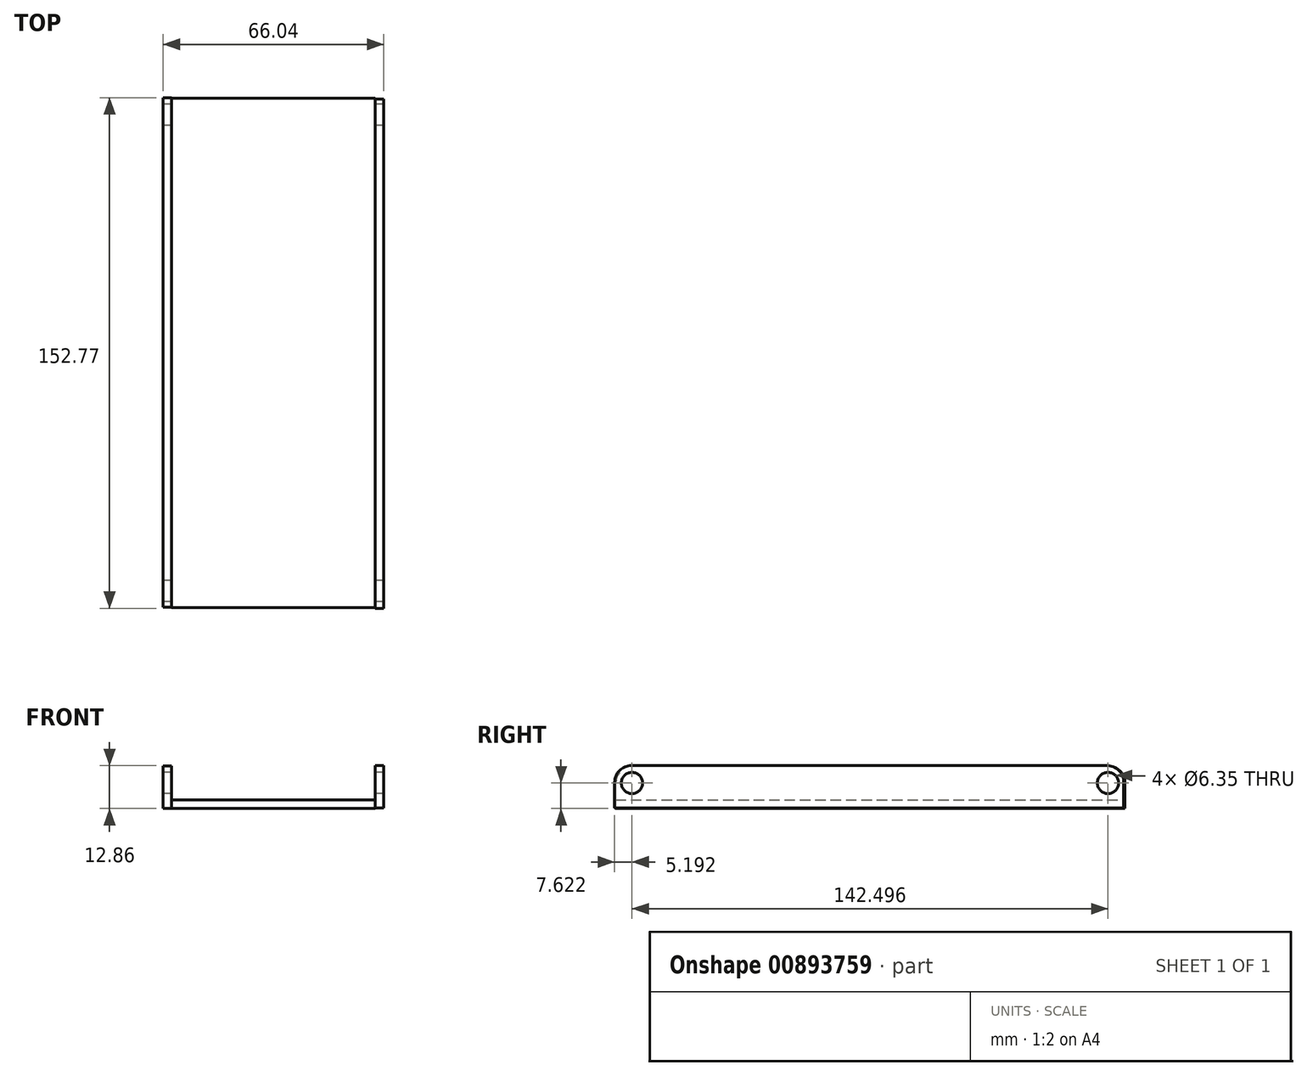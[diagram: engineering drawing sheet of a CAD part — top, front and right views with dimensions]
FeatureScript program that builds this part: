
annotation { "Feature Type Name" : "Feature", "Feature Type Description" : "" }
export const myFeature = defineFeature(function(context is Context, id is Id, definition is map)
    precondition{}
    {
        {
            var Q0;
            Q0=qCreatedBy(makeId("Top.planeOp"),FACE);
            var sketch = newSketch(context, id + "F0", { "sketchPlane" : qUnion([Q0])});
            skLineSegment(sketch, "E0.bottom", {"start": v(30.48, -76.2) * mm, "end": v(-30.48, -76.2) * mm});
            skLineSegment(sketch, "E0.top", {"start": v(30.48, 76.2) * mm, "end": v(-30.48, 76.2) * mm});
            skLineSegment(sketch, "E0.left", {"start": v(30.48, -76.2) * mm, "end": v(30.48, 76.2) * mm});
            skLineSegment(sketch, "E0.right", {"start": v(-30.48, -76.2) * mm, "end": v(-30.48, 76.2) * mm});
            skPoint(sketch, "E0.middle", {"position": v(0, 0) * mm});
            skSolve(sketch);
        }
        {
            var Q0;
            Q0=qSketchRegion(id+"F0",true);
            extrude(context, id + "F1", {"entities" : qUnion([Q0]), "depth" : 2.54 * mm, "offsetDistance" : 25.4 * mm});
        }
        {
            var Q0;
            Q0=makeQuery(id+"F1.opExtrude","SWEPT_FACE",FACE,{"disambiguationData":[OSD([sQuery(id+"F0.wireOp",EDGE,"E0.left")])]});
            var sketch = newSketch(context, id + "F2", { "sketchPlane" : qUnion([Q0])});
            skLineSegment(sketch, "E1.bottom", {"start": v(75.96, 0.1) * mm, "end": v(-76.44, 0.1) * mm});
            skLineSegment(sketch, "E1.top", {"start": v(75.96, 12.8) * mm, "end": v(-76.44, 12.8) * mm});
            skLineSegment(sketch, "E1.left", {"start": v(75.96, 0.1) * mm, "end": v(75.96, 12.8) * mm});
            skLineSegment(sketch, "E1.right", {"start": v(-76.44, 0.1) * mm, "end": v(-76.44, 12.8) * mm});
            skPoint(sketch, "E1.middle", {"position": v(-0.24, 6.45) * mm});
            skSolve(sketch);
        }
        {
            var Q0;
            Q0=qSketchRegion(id+"F2",true);
            extrude(context, id + "F3", {"entities" : qUnion([Q0]), "operationType" : NewBodyOperationType.ADD, "depth" : 2.54 * mm, "offsetDistance" : 25.4 * mm});
        }
        {
            var Q0;
            Q0=makeQuery(id+"F1.opExtrude","SWEPT_FACE",FACE,{"disambiguationData":[OSD([sQuery(id+"F0.wireOp",EDGE,"E0.right")])]});
            var sketch = newSketch(context, id + "F4", { "sketchPlane" : qUnion([Q0])});
            skLineSegment(sketch, "E2.bottom", {"start": v(76.07, -0.06) * mm, "end": v(-76.33, -0.06) * mm});
            skLineSegment(sketch, "E2.top", {"start": v(76.07, 12.64) * mm, "end": v(-76.33, 12.64) * mm});
            skLineSegment(sketch, "E2.left", {"start": v(76.07, -0.06) * mm, "end": v(76.07, 12.64) * mm});
            skLineSegment(sketch, "E2.right", {"start": v(-76.33, -0.06) * mm, "end": v(-76.33, 12.64) * mm});
            skPoint(sketch, "E2.middle", {"position": v(-0.13, 6.3) * mm});
            skSolve(sketch);
        }
        {
            var Q0;
            Q0=qSketchRegion(id+"F4",true);
            extrude(context, id + "F5", {"entities" : qUnion([Q0]), "operationType" : NewBodyOperationType.ADD, "depth" : 2.54 * mm, "offsetDistance" : 25.4 * mm});
        }
        {
            var Q0;
            Q0=makeQuery(id+"F3.opExtrude","SWEPT_EDGE",EDGE,{"disambiguationData":[OSD([sQuery(id+"F2.wireOp",EDGE,"E1.top"),sQuery(id+"F2.wireOp",EDGE,"E1.right")])]});
            var Q1;
            Q1=makeQuery(id+"F5.opExtrude","SWEPT_EDGE",EDGE,{"disambiguationData":[OSD([sQuery(id+"F4.wireOp",EDGE,"E2.top"),sQuery(id+"F4.wireOp",EDGE,"E2.left")])]});
            var Q2;
            Q2=makeQuery(id+"F3.opExtrude","SWEPT_EDGE",EDGE,{"disambiguationData":[OSD([sQuery(id+"F2.wireOp",EDGE,"E1.top"),sQuery(id+"F2.wireOp",EDGE,"E1.left")])]});
            var Q3;
            Q3=makeQuery(id+"F5.opExtrude","SWEPT_EDGE",EDGE,{"disambiguationData":[OSD([sQuery(id+"F4.wireOp",EDGE,"E2.top"),sQuery(id+"F4.wireOp",EDGE,"E2.right")])]});
            fillet(context, id + "F6", {"entities" : qUnion([Q0, Q1, Q2, Q3]), "radius" : 5.08 * mm, "tangentPropagation" : true, "allowEdgeOverflow" : false});
        }
        {
            var Q0;
            Q0=makeQuery(id+"F5.opExtrude","CAP_FACE",FACE,{"disambiguationData":[OSD([sQuery(id+"F4.wireOp",EDGE,"E2.bottom"),sQuery(id+"F4.wireOp",EDGE,"E2.top"),sQuery(id+"F4.wireOp",EDGE,"E2.left"),sQuery(id+"F4.wireOp",EDGE,"E2.right")])],"isStart":false});
            var sketch = newSketch(context, id + "F7", { "sketchPlane" : qUnion([Q0])});
            skCircle(sketch, "E3", {"center": v(-71.25, 7.56) * mm, "radius": 3.18 * mm});
            skCircle(sketch, "E4.MirrorC", {"center": v(71.25, 7.56) * mm, "radius": 3.18 * mm});
            skSolve(sketch);
        }
        {
            var Q0;
            Q0=qSketchRegion(id+"F7",true);
            extrude(context, id + "F8", {"entities" : qUnion([Q0]), "operationType" : NewBodyOperationType.REMOVE, "oppositeDirection" : true, "depth" : 90.17 * mm, "offsetDistance" : 25.4 * mm});
        }
    });
